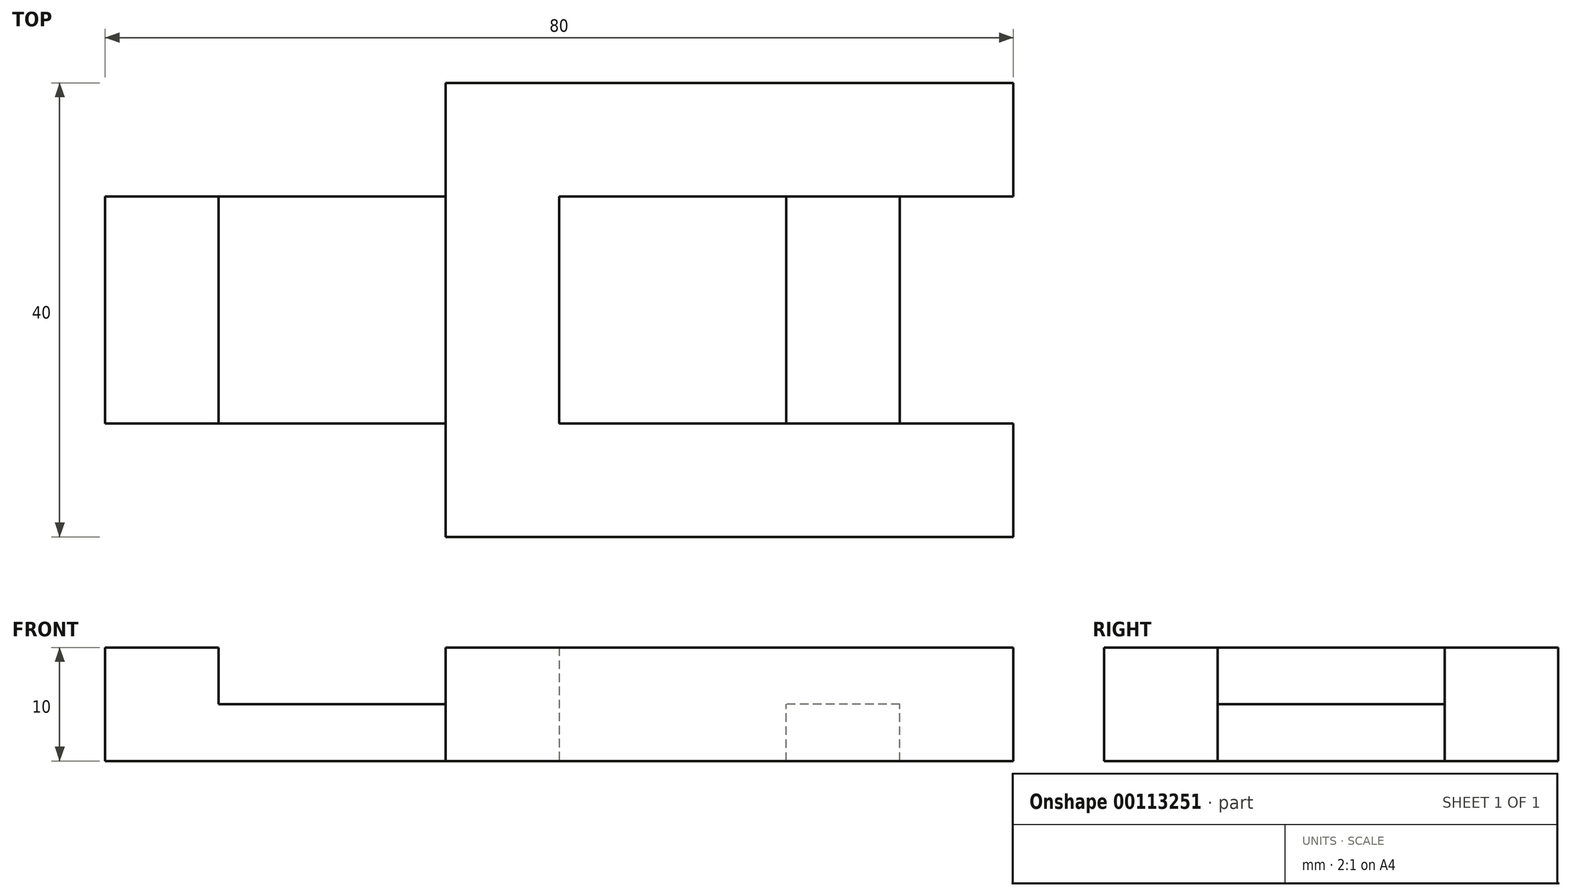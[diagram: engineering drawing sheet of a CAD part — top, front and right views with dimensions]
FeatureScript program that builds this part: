
annotation { "Feature Type Name" : "Feature", "Feature Type Description" : "" }
export const myFeature = defineFeature(function(context is Context, id is Id, definition is map)
    precondition{}
    {
        {
            var Q0;
            Q0=qCreatedBy(makeId("Front.planeOp"),FACE);
            var sketch = newSketch(context, id + "F0", { "sketchPlane" : qUnion([Q0])});
            skLineSegment(sketch, "E0", {"start": v(0, 0) * mm, "end": v(0, 10) * mm});
            skLineSegment(sketch, "E1", {"start": v(0, 10) * mm, "end": v(10, 10) * mm});
            skLineSegment(sketch, "E2", {"start": v(10, 10) * mm, "end": v(10, 5) * mm});
            skLineSegment(sketch, "E3", {"start": v(40, 5) * mm, "end": v(10, 5) * mm});
            skLineSegment(sketch, "E4", {"start": v(40, 5) * mm, "end": v(40, 10) * mm});
            skLineSegment(sketch, "E5", {"start": v(40, 10) * mm, "end": v(80, 10) * mm});
            skLineSegment(sketch, "E6", {"start": v(80, 10) * mm, "end": v(80, 0) * mm});
            skLineSegment(sketch, "E7", {"start": v(80, 0) * mm, "end": v(0, 0) * mm});
            skSolve(sketch);
        }
        {
            var Q0;
            Q0 = qSketchRegion(id + "F0", true);
            extrude(context, id + "F1", {"entities" : qUnion([Q0]), "depth" : 40 * mm});
        }
        {
            var Q0;
            Q0=makeQuery(id+"F1.opExtrude","CAP_FACE",FACE,{"disambiguationData":[OSD([sQuery(id+"F0.wireOp",EDGE,"E0"),sQuery(id+"F0.wireOp",EDGE,"E1"),sQuery(id+"F0.wireOp",EDGE,"E2"),sQuery(id+"F0.wireOp",EDGE,"E3"),sQuery(id+"F0.wireOp",EDGE,"E4"),sQuery(id+"F0.wireOp",EDGE,"E5"),sQuery(id+"F0.wireOp",EDGE,"E6"),sQuery(id+"F0.wireOp",EDGE,"E7")])],"isStart":false});
            var sketch = newSketch(context, id + "F2", { "sketchPlane" : qUnion([Q0])});
            skLineSegment(sketch, "E8.0", {"start": v(0, 10) * mm, "end": v(10, 10) * mm});
            skLineSegment(sketch, "E9.0", {"start": v(0, 0) * mm, "end": v(0, 10) * mm});
            skLineSegment(sketch, "E10.0", {"start": v(80, 0) * mm, "end": v(0, 0) * mm});
            skLineSegment(sketch, "E11.0", {"start": v(40, 5) * mm, "end": v(10, 5) * mm});
            skLineSegment(sketch, "E12.0", {"start": v(10, 10) * mm, "end": v(10, 5) * mm});
            skLineSegment(sketch, "E13.0", {"start": v(40, 5) * mm, "end": v(40, 10) * mm});
            skLineSegment(sketch, "E14", {"start": v(40, 5) * mm, "end": v(40, 0) * mm});
            skSolve(sketch);
        }
        {
            var Q0;
            Q0 = qSketchRegion(id + "F2", true);
            extrude(context, id + "F3", {"entities" : qUnion([Q0]), "operationType" : NewBodyOperationType.REMOVE, "oppositeDirection" : true, "depth" : 10 * mm});
        }
        {
            var Q0;
            Q0=makeQuery(id+"F1.opExtrude","CAP_FACE",FACE,{"disambiguationData":[OSD([sQuery(id+"F0.wireOp",EDGE,"E0"),sQuery(id+"F0.wireOp",EDGE,"E1"),sQuery(id+"F0.wireOp",EDGE,"E2"),sQuery(id+"F0.wireOp",EDGE,"E3"),sQuery(id+"F0.wireOp",EDGE,"E4"),sQuery(id+"F0.wireOp",EDGE,"E5"),sQuery(id+"F0.wireOp",EDGE,"E6"),sQuery(id+"F0.wireOp",EDGE,"E7")])],"isStart":true});
            var sketch = newSketch(context, id + "F4", { "sketchPlane" : qUnion([Q0])});
            skLineSegment(sketch, "E15.0", {"start": v(0, 0) * mm, "end": v(0, 10) * mm});
            skLineSegment(sketch, "E16.0", {"start": v(0, 10) * mm, "end": v(-10, 10) * mm});
            skLineSegment(sketch, "E17.0", {"start": v(-80, 0) * mm, "end": v(0, 0) * mm});
            skLineSegment(sketch, "E18.0", {"start": v(-40, 5) * mm, "end": v(-10, 5) * mm});
            skLineSegment(sketch, "E19", {"start": v(-40, 5) * mm, "end": v(-40, 0) * mm});
            skSolve(sketch);
        }
        {
            var Q0;
            {var subQ1=sQuery(id+"F4.wireOp",EDGE,"E15.0");Q0=makeQuery(id+"F4.imprint","IMPRINT",FACE,{"disambiguationData":[TD([[makeQuery(id+"F4.imprint","IMPRINT",EDGE,{"derivedFrom":subQ1}),1.0]])]});}
            extrude(context, id + "F5", {"entities" : qUnion([Q0]), "operationType" : NewBodyOperationType.REMOVE, "oppositeDirection" : true, "depth" : 10 * mm});
        }
        {
            var Q0;
            Q0=makeQuery(id+"F1.opExtrude","SWEPT_FACE",FACE,{"disambiguationData":[OSD([sQuery(id+"F0.wireOp",EDGE,"E5")])]});
            var sketch = newSketch(context, id + "F6", { "sketchPlane" : qUnion([Q0])});
            skLineSegment(sketch, "E20.0", {"start": v(40, -40) * mm, "end": v(80, -40) * mm});
            skLineSegment(sketch, "E21.0.0", {"start": v(80, 0) * mm, "end": v(40, 0) * mm});
            skLineSegment(sketch, "E21.0.1", {"start": v(40, 0) * mm, "end": v(40, -40) * mm});
            skLineSegment(sketch, "E21.0.3", {"start": v(80, -40) * mm, "end": v(80, 0) * mm});
            skPoint(sketch, "E22.0", {"position": v(0, -30) * mm});
            skPoint(sketch, "E23.0", {"position": v(0, -10) * mm});
            skLineSegment(sketch, "E24", {"start": v(80, -30) * mm, "end": v(70, -30) * mm});
            skLineSegment(sketch, "E25", {"start": v(70, -30) * mm, "end": v(70, -10) * mm});
            skLineSegment(sketch, "E26", {"start": v(70, -10) * mm, "end": v(80, -10) * mm});
            skLineSegment(sketch, "E27", {"start": v(70, -30) * mm, "end": v(40, -30) * mm});
            skLineSegment(sketch, "E28", {"start": v(70, -10) * mm, "end": v(40, -10) * mm});
            skSolve(sketch);
        }
        {
            var Q0;
            {var subQ0=sQuery(id+"F6.wireOp",EDGE,"E24");Q0=makeQuery(id+"F6.imprint","IMPRINT",FACE,{"disambiguationData":[TD([[makeQuery(id+"F6.imprint","IMPRINT",EDGE,{"derivedFrom":subQ0}),-1.0]])]});}
            extrude(context, id + "F7", {"entities" : qUnion([Q0]), "operationType" : NewBodyOperationType.REMOVE, "oppositeDirection" : true, "depth" : 25 * mm});
        }
        {
            var Q0;
            Q0=makeQuery(id+"F6.imprint","IMPRINT",FACE,{"disambiguationData":[TD([[makeQuery(id+"F6.imprint","IMPRINT",EDGE,{"derivedFrom":sQuery(id+"F6.wireOp",EDGE,"E25")}),1.0]])]});
            extrude(context, id + "F8", {"entities" : qUnion([Q0]), "operationType" : NewBodyOperationType.REMOVE, "oppositeDirection" : true, "depth" : 5 * mm});
        }
        {
            var Q0;
            {var subQ2=sQuery(id+"F0.wireOp",EDGE,"E5");Q0=makeQuery(id+"F8.boolean.opBoolean","SPLIT",FACE,{"disambiguationData":[TD([makeQuery(id+"F7.boolean.opBoolean","COPY",FACE,{"derivedFrom":makeQuery(id+"F7.opExtrude","SWEPT_FACE",FACE,{"disambiguationData":[OSD([sQuery(id+"F6.wireOp",EDGE,"E24")])]})})])],"derivedFrom":makeQuery(id+"F1.opExtrude","SWEPT_FACE",FACE,{"disambiguationData":[OSD([subQ2])]})});}
            var sketch = newSketch(context, id + "F9", { "sketchPlane" : qUnion([Q0])});
            skLineSegment(sketch, "E29", {"start": v(40, -40) * mm, "end": v(30, -40) * mm});
            skLineSegment(sketch, "E30", {"start": v(30, -40) * mm, "end": v(30, 0) * mm});
            skLineSegment(sketch, "E31", {"start": v(30, 0) * mm, "end": v(40, 0) * mm});
            skLineSegment(sketch, "E32", {"start": v(40, 0) * mm, "end": v(40, -40) * mm});
            skLineSegment(sketch, "E33", {"start": v(40, -30) * mm, "end": v(60, -30) * mm});
            skLineSegment(sketch, "E34.0", {"start": v(40, -10) * mm, "end": v(80, -10) * mm});
            skLineSegment(sketch, "E35", {"start": v(60, -30) * mm, "end": v(60, -10) * mm});
            skSolve(sketch);
        }
        {
            var Q0;
            {var subQ0=sQuery(id+"F9.wireOp",EDGE,"E33");Q0=makeQuery(id+"F9.imprint","IMPRINT",FACE,{"disambiguationData":[TD([[makeQuery(id+"F9.imprint","IMPRINT",EDGE,{"derivedFrom":subQ0}),-1.0]])]});}
            extrude(context, id + "F10", {"entities" : qUnion([Q0]), "operationType" : NewBodyOperationType.REMOVE, "oppositeDirection" : true, "depth" : 25 * mm});
        }
        {
            var Q0;
            {var subQ3=sQuery(id+"F9.wireOp",EDGE,"E29");Q0=makeQuery(id+"F9.imprint","IMPRINT",FACE,{"disambiguationData":[TD([[makeQuery(id+"F9.imprint","IMPRINT",EDGE,{"derivedFrom":subQ3}),-1.0]])]});}
            extrude(context, id + "F11", {"entities" : qUnion([Q0]), "operationType" : NewBodyOperationType.ADD, "oppositeDirection" : true, "depth" : 10 * mm});
        }
    });
